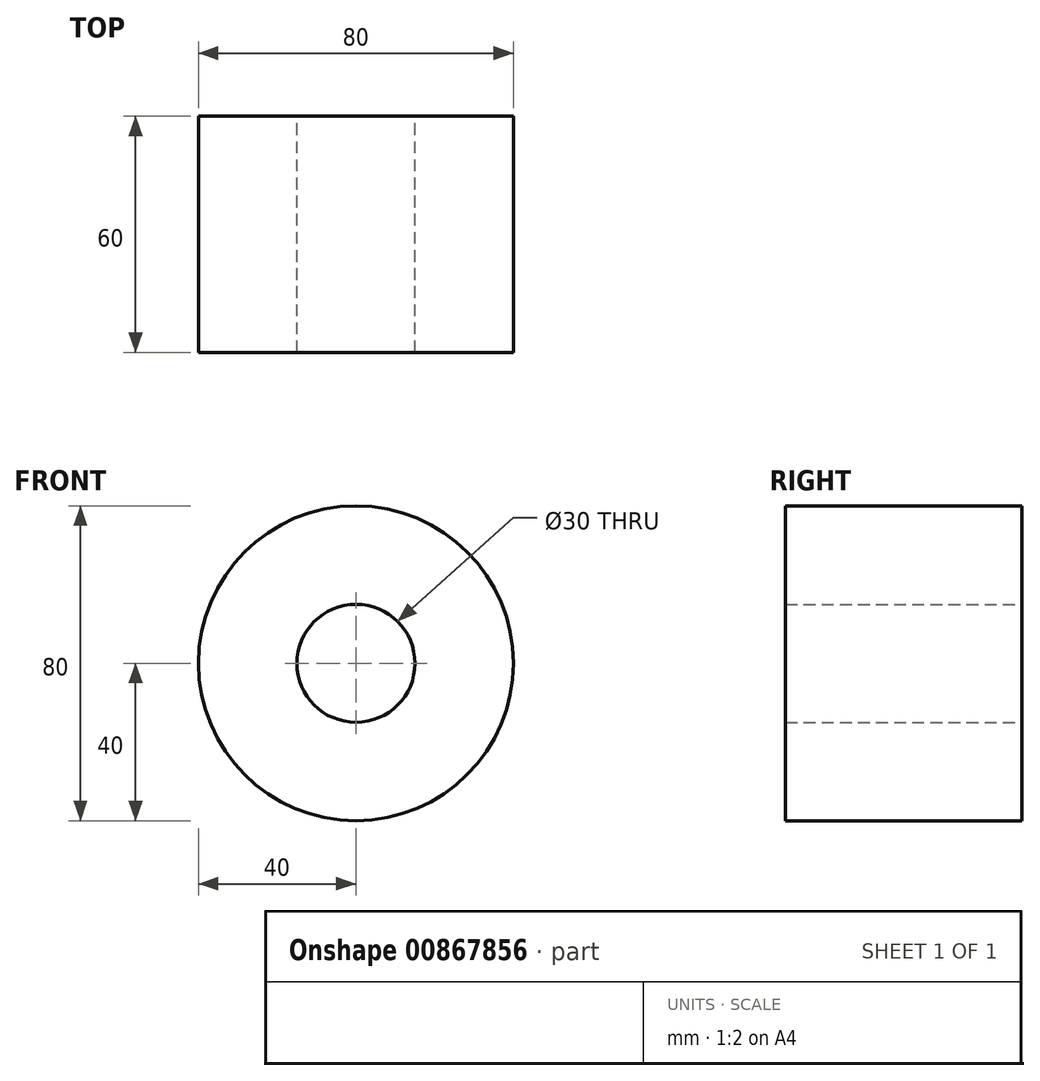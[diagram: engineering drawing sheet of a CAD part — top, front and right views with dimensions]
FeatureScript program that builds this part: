
annotation { "Feature Type Name" : "Feature", "Feature Type Description" : "" }
export const myFeature = defineFeature(function(context is Context, id is Id, definition is map)
    precondition{}
    {
        {
            var Q0;
            Q0=qCreatedBy(makeId("Front.planeOp"),FACE);
            var sketch = newSketch(context, id + "F0", { "sketchPlane" : qUnion([Q0])});
            skCircle(sketch, "E0", {"center": v(0, 0) * mm, "radius": 40 * mm});
            skCircle(sketch, "E1", {"center": v(0, 0) * mm, "radius": 15 * mm});
            skSolve(sketch);
        }
        {
            var Q0;
            Q0=makeQuery(id+"F0.imprint","IMPRINT",FACE,{"disambiguationData":[TD([[makeQuery(id+"F0.imprint","IMPRINT",EDGE,{"derivedFrom":sQuery(id+"F0.wireOp",EDGE,"E0")}),1.0]])]});
            extrude(context, id + "F1", {"entities" : qUnion([Q0]), "depth" : 60 * mm, "offsetDistance" : 25 * mm});
        }
    });
